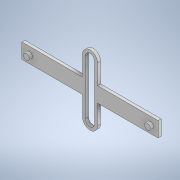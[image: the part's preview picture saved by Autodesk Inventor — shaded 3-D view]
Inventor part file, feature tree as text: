
AUTODESK INVENTOR PART (.ipt)
format: ipt  version: 2022 (Build 260153000, 153)  size: 135,168 bytes
history: native  units: mm
features: extrude x3, sketch x3, mirror x1
ambient origin geometry x8: Origin, YZ Plane, XZ Plane, XY Plane, X Axis, Y Axis, Z Axis, Center Point
bodies: Body1 (feature_tree)
feature tree (7):
  extrude  "돌출3"  Depth=18.0mm
  extrude  "돌출4"  Depth=1.5mm
  extrude  "돌출5"  Depth=1.0mm
  mirror  "미러1"
  sketch  "스케치3"
  sketch  "스케치4"
  sketch  "스케치5"
